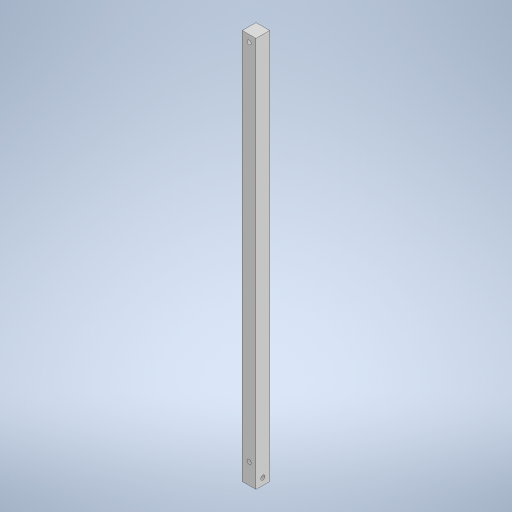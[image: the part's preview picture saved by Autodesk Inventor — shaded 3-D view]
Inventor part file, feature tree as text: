
AUTODESK INVENTOR PART (.ipt)
format: ipt  version: 2023 (Build 270158000, 158)  size: 249,344 bytes
history: native  units: mm
features: sketch x3, hole x2, other x1, extrude x1
ambient origin geometry x8: Origin, YZ Plane, XZ Plane, XY Plane, X Axis, Y Axis, Z Axis, Center Point
bodies: Body1 (feature_tree)
feature tree (7):
  other  "ソリッド1"
  extrude  "押し出し1"  Depth=10.0mm
  hole  "穴1"  [1 undecoded]
  hole  "穴2"  [1 undecoded]
  sketch  "スケッチ1"
  sketch  "スケッチ2"
  sketch  "スケッチ3"
note: 2 required parameter values undecoded (feature->parameter linkage not recoverable at this tier; creation-order binding heuristic only, values carry confidence <= 0.55)
